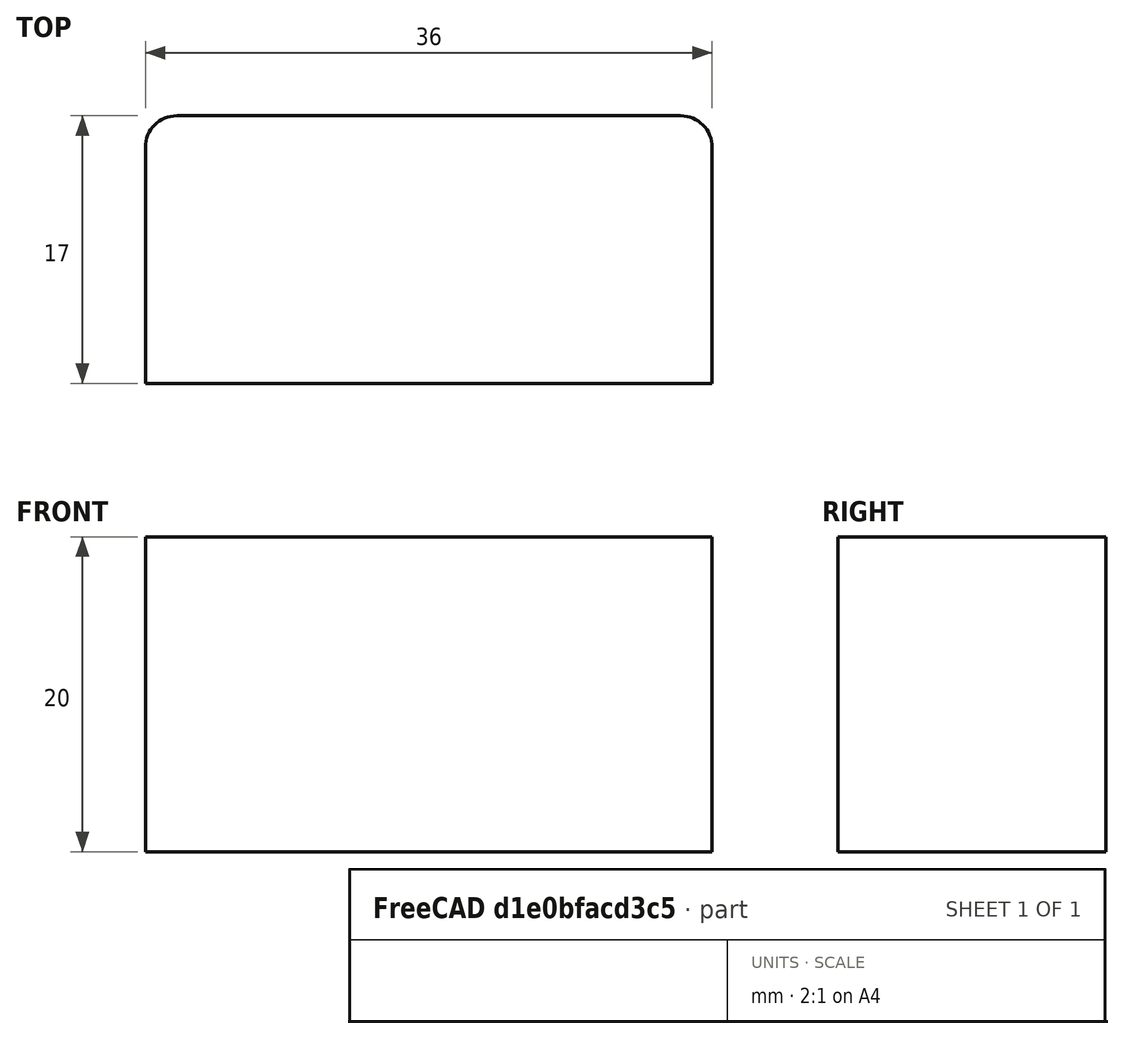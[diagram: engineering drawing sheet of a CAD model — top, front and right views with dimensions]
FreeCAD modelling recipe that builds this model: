
FCSTD DOCUMENT  (FreeCAD 1.0R39109 (Git))
Label: Open Sticky Mount
License: All rights reserved
LicenseURL: http://en.wikipedia.org/wiki/All_rights_reserved
objects: Sketcher::SketchObject×2, Spreadsheet::Sheet×1, PartDesign::Pad×1, PartDesign::Body×1
note: 8 computed .brp shape members not serialized (recipe doc carries the construction recipe); baked Part::Feature solids carry a one-line shape summary decoded from their .brp

FEATURE [Spreadsheet::Sheet] Spreadsheet
  cells = A1='bar_diameter; B1(bar_diameter)=28; A2='bottom_thickness; B2(bottom_thickness)=1; A3='side_thickness; B3(side_thickness)=4; A4='back_thickness; B4(back_thickness)=1; A5='top_fillet_radius; B5(top_fillet_radius)=1; A6='depth; B6(depth)=20
FEATURE [Sketcher::SketchObject] Sketch
  ArcFitTolerance = 1e-06
  AttachmentSupport = -> [XY_Plane]
  FullyConstrained = true
  MakeInternals = false
  MapMode = 5
  expr: Constraints[13] = Spreadsheet.bar_diameter + Spreadsheet.side_thickness * 2
  expr: Constraints[14] = Spreadsheet.side_thickness
  expr: Constraints[15] = Spreadsheet.side_thickness
  expr: Constraints[17] = Spreadsheet.bar_diameter / 2 + Spreadsheet.bottom_thickness
  sketch-geometry (6):
    g0: LineSegment StartX=0 StartY=0 StartZ=0 EndX=0 EndY=15 EndZ=0
    g1: LineSegment StartX=36 StartY=15 StartZ=0 EndX=36 EndY=0 EndZ=0
    g2: LineSegment StartX=0 StartY=0 StartZ=0 EndX=36 EndY=0 EndZ=0
    g3: ArcOfCircle CenterX=2 CenterY=15 CenterZ=0 NormalX=0 NormalY=0 NormalZ=1 AngleXU=0 Radius=2 StartAngle=1.5708 EndAngle=3.14159
    g4: ArcOfCircle CenterX=34 CenterY=15 CenterZ=0 NormalX=0 NormalY=0 NormalZ=1 AngleXU=0 Radius=2 StartAngle=0 EndAngle=1.5708
    g5: LineSegment StartX=2 StartY=17 StartZ=0 EndX=34 EndY=17 EndZ=0
  constraints (19):
    c: Coincident(g0,g-1)
    c: Vertical(g0)
    c: Vertical(g1)
    c: Coincident(g2,g0)
    c: Coincident(g2,g1)
    c: Horizontal(g2)
    c: Coincident(g3,g0)
    c: Coincident(g4,g1)
    c: Coincident(g5,g3)
    c: Coincident(g5,g4)
    c: Horizontal(g5)
    c: Horizontal(g3,g0)
    c: Horizontal(g4,g1)
    c: DistanceX(g2,g2) = 36
    c: Diameter(g3) = 4
    c: Diameter(g4) = 4
    c: Vertical(g3,g3)
    c: DistanceY(g0,g3) = 15
    c: Vertical(g4,g4)
FEATURE [PartDesign::Pad] Pad
  Direction = (0,0,1)
  Length = 20
  Length2 = 10
  Profile = -> Sketch
  ReferenceAxis = -> Sketch [N_Axis]
  Suppressed = false
  Type = 0
  expr: Length = Spreadsheet.depth
FEATURE [Sketcher::SketchObject] Sketch001
  ArcFitTolerance = 1e-06
  AttachmentSupport = -> [Pad]
  FullyConstrained = false
  MakeInternals = false
  MapMode = 5
  Placement = pos=(0,0,20) rot=(0,0,1;0rad)
  expr: Constraints[0] = Spreadsheet.bar_diameter / 2 + Spreadsheet.bottom_thickness
  expr: Constraints[8] = Spreadsheet.side_thickness
  expr: Constraints[9] = Spreadsheet.side_thickness
  sketch-geometry (4):
    g0: ArcOfCircle CenterX=18.0088 CenterY=15 CenterZ=0 NormalX=0 NormalY=0 NormalZ=1 AngleXU=0 Radius=14.0036 StartAngle=3.14159 EndAngle=6.28336
    g1: ArcOfCircle CenterX=2.00522 CenterY=14.9893 CenterZ=0 NormalX=0 NormalY=0 NormalZ=1 AngleXU=0 Radius=2 StartAngle=0.00536317 EndAngle=1.5708
    g2: ArcOfCircle CenterX=34.0124 CenterY=14.9893 CenterZ=0 NormalX=0 NormalY=0 NormalZ=1 AngleXU=0 Radius=2 StartAngle=1.5708 EndAngle=3.13504
    g3: LineSegment StartX=2.00522 StartY=16.9893 StartZ=0 EndX=34.0124 EndY=16.9893 EndZ=0
  constraints (10):
    c: DistanceY(g-1,g0) = 15
    c: Coincident(g1,g0)
    c: Coincident(g2,g0)
    c: Coincident(g3,g1)
    c: Coincident(g3,g2)
    c: Horizontal(g3)
    c: Vertical(g2,g2)
    c: Vertical(g1,g1)
    c: Diameter(g1) = 4
    c: Diameter(g2) = 4
FEATURE [PartDesign::Body] Body
  AllowCompound = false
  Group = -> [Sketch,Pad,Sketch001]
  Origin = -> Origin
  Tip = -> Pad
